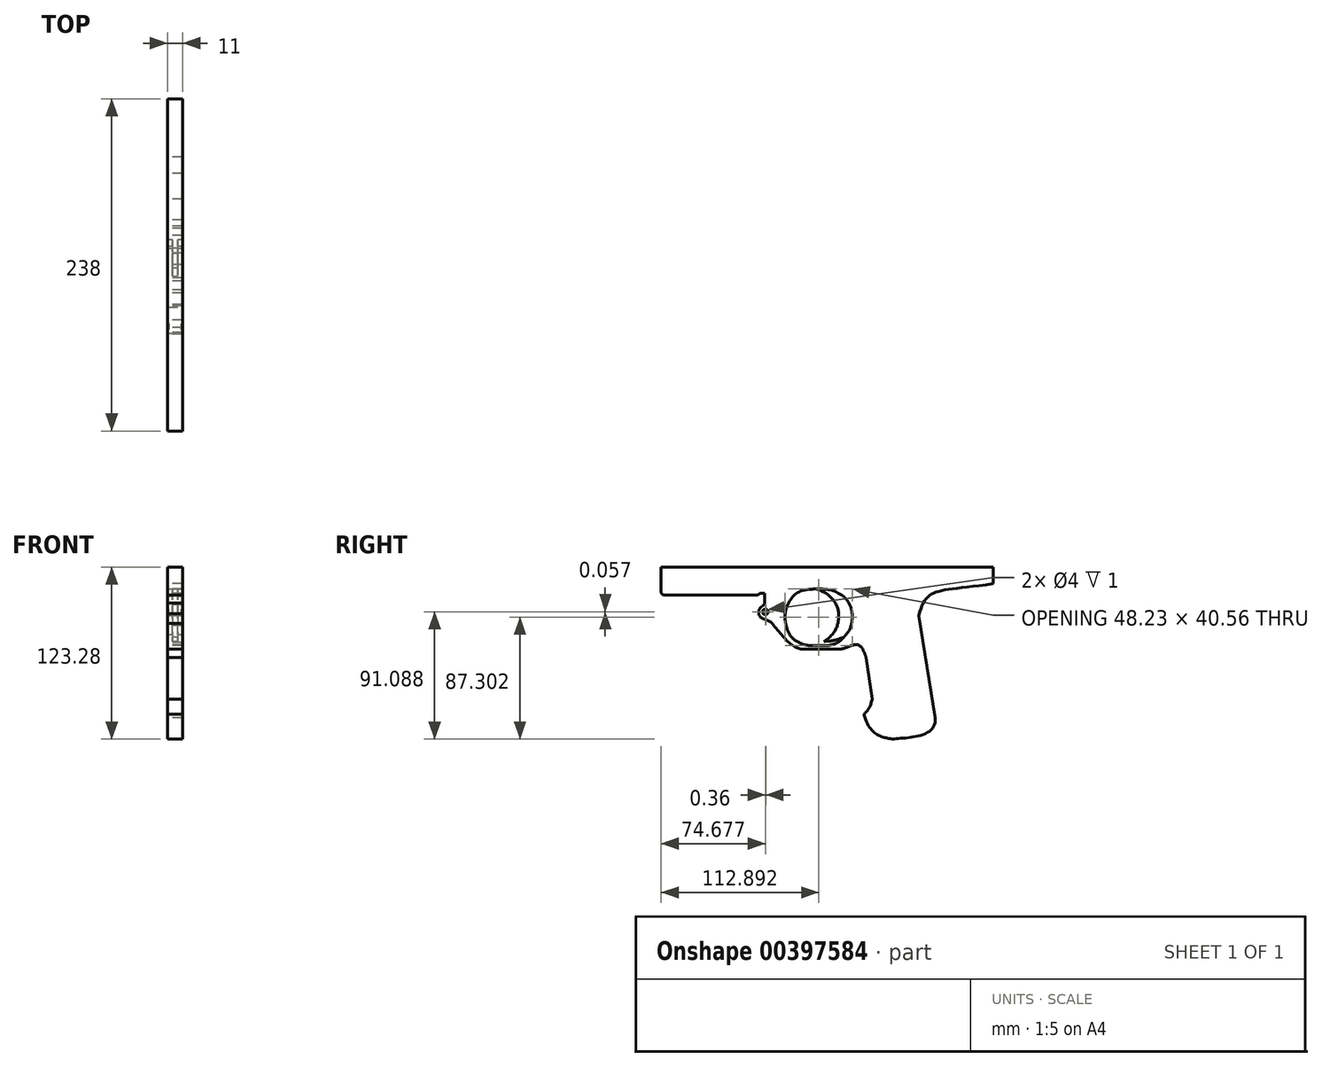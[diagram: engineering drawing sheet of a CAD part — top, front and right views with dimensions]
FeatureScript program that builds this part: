
annotation { "Feature Type Name" : "Feature", "Feature Type Description" : "" }
export const myFeature = defineFeature(function(context is Context, id is Id, definition is map)
    precondition{}
    {
        {
            var Q0;
            Q0=qCreatedBy(makeId("Right.planeOp"),FACE);
            var sketch = newSketch(context, id + "F0", { "sketchPlane" : qUnion([Q0])});
            skLineSegment(sketch, "E0", {"start": v(0, 0) * mm, "end": v(0, -230) * mm});
            skLineSegment(sketch, "E1", {"start": v(0, -230) * mm, "end": v(119.99, -230) * mm});
            skLineSegment(sketch, "E2", {"start": v(0, -230) * mm, "end": v(-112.03, -230) * mm});
            skLineSegment(sketch, "E3", {"start": v(-112.03, -230) * mm, "end": v(125.97, -230) * mm});
            skLineSegment(sketch, "E4.bottom", {"start": v(125.97, -230) * mm, "end": v(-112.03, -230) * mm});
            skLineSegment(sketch, "E4.top", {"start": v(125.97, -218) * mm, "end": v(-112.03, -218) * mm});
            skLineSegment(sketch, "E4.left", {"start": v(125.97, -230) * mm, "end": v(125.97, -218) * mm});
            skLineSegment(sketch, "E4.right", {"start": v(-112.03, -230) * mm, "end": v(-112.03, -218) * mm});
            skLineSegment(sketch, "E5.bottom", {"start": v(-112.03, -230) * mm, "end": v(-42.58, -230) * mm});
            skLineSegment(sketch, "E5.top", {"start": v(-112.03, -238) * mm, "end": v(-42.58, -238) * mm});
            skLineSegment(sketch, "E5.left", {"start": v(-112.03, -230) * mm, "end": v(-112.03, -238) * mm});
            skLineSegment(sketch, "E5.right", {"start": v(-42.58, -230) * mm, "end": v(-42.58, -238) * mm});
            skFitSpline(sketch, "E6", {"points": [v(125.97, -230) * mm, v(72.63, -252.96) * mm], "startDerivative": vector(-124.55, -18.11) * mm, "endDerivative": vector(-16.76, -64.23) * mm});
            skLineSegment(sketch, "E7", {"start": v(72.63, -252.96) * mm, "end": v(84.38, -326.13) * mm});
            skLineSegment(sketch, "E8", {"start": v(72.63, -252.96) * mm, "end": v(30.63, -252.96) * mm});
            skLineSegment(sketch, "E9", {"start": v(30.63, -252.96) * mm, "end": v(39.17, -312.77) * mm});
            skFitSpline(sketch, "E10", {"points": [v(39.17, -312.77) * mm, v(33.3, -323.55) * mm], "startDerivative": vector(-4.85, -23.29) * mm, "endDerivative": vector(-3.71, -4.12) * mm});
            skFitSpline(sketch, "E11", {"points": [v(33.3, -323.55) * mm, v(54.05, -341.28) * mm], "startDerivative": vector(11.13, -45.76) * mm, "endDerivative": vector(21.03, -2.47) * mm});
            skFitSpline(sketch, "E12", {"points": [v(54.05, -341.28) * mm, v(84.38, -326.13) * mm], "startDerivative": vector(26.38, 2.89) * mm, "endDerivative": vector(-5.07, 44.22) * mm});
            skFitSpline(sketch, "E13", {"points": [v(34.9, -282.87) * mm, v(28.31, -273.6) * mm], "startDerivative": vector(-4.14, 7.9) * mm, "endDerivative": vector(-14.15, 4) * mm});
            skFitSpline(sketch, "E14", {"points": [v(28.31, -273.6) * mm, v(15.3, -276.86) * mm], "startDerivative": vector(-16.78, -0.73) * mm, "endDerivative": vector(-15.09, 0.25) * mm});
            skLineSegment(sketch, "E15", {"start": v(15.3, -276.86) * mm, "end": v(-10.85, -276.86) * mm});
            skFitSpline(sketch, "E16", {"points": [v(-10.85, -276.86) * mm, v(-32.4, -258.45) * mm], "startDerivative": vector(-21.55, 1.34) * mm, "endDerivative": vector(-21.06, 27.43) * mm});
            skFitSpline(sketch, "E17", {"points": [v(-32.4, -258.45) * mm, v(-42.03, -251.43) * mm], "startDerivative": vector(-13.71, 13.22) * mm, "endDerivative": vector(-3.43, 15.67) * mm});
            skFitSpline(sketch, "E18", {"points": [v(-42.03, -251.43) * mm, v(-37.79, -243.92) * mm], "startDerivative": vector(-1.47, 16.65) * mm, "endDerivative": vector(1.96, 8.33) * mm});
            skLineSegment(sketch, "E19", {"start": v(-37.79, -243.92) * mm, "end": v(-37.79, -236.74) * mm});
            skLineSegment(sketch, "E20", {"start": v(-37.79, -236.74) * mm, "end": v(-41.22, -236.74) * mm});
            skLineSegment(sketch, "E21", {"start": v(-41.22, -236.74) * mm, "end": v(-42.58, -238) * mm});
            skFitSpline(sketch, "E22", {"points": [v(-2.29, -233.8) * mm, v(-21.4, -245.26) * mm], "startDerivative": vector(-13.28, -0.6) * mm, "endDerivative": vector(-14.49, -35) * mm});
            skFitSpline(sketch, "E23", {"points": [v(-21.4, -245.26) * mm, v(-22.36, -259.94) * mm], "startDerivative": vector(-6.68, -12.56) * mm, "endDerivative": vector(4.15, -12.1) * mm});
            skFitSpline(sketch, "E24", {"points": [v(-22.36, -259.94) * mm, v(-13.25, -272.16) * mm], "startDerivative": vector(3.8, -18.33) * mm, "endDerivative": vector(14.87, -6.57) * mm});
            skFitSpline(sketch, "E25", {"points": [v(-13.25, -272.16) * mm, v(-4.64, -274.26) * mm], "startDerivative": vector(13.14, -6.31) * mm, "endDerivative": vector(7.97, -0.18) * mm});
            skLineSegment(sketch, "E26", {"start": v(-4.64, -274.26) * mm, "end": v(7.27, -274.26) * mm});
            skFitSpline(sketch, "E27", {"points": [v(7.27, -274.26) * mm, v(20.33, -266.59) * mm], "startDerivative": vector(21.47, 2.35) * mm, "endDerivative": vector(8.86, 11) * mm});
            skFitSpline(sketch, "E28", {"points": [v(20.33, -266.59) * mm, v(24.98, -253.08) * mm], "startDerivative": vector(11, 12.08) * mm, "endDerivative": vector(0.54, 16.64) * mm});
            skFitSpline(sketch, "E29", {"points": [v(24.98, -253.08) * mm, v(18.54, -239.13) * mm], "startDerivative": vector(-0.8, 17.17) * mm, "endDerivative": vector(-13.42, 11) * mm});
            skFitSpline(sketch, "E30", {"points": [v(18.54, -239.13) * mm, v(5.48, -233.94) * mm, v(-2.29, -233.8) * mm], "startDerivative": vector(-32.75, 23.86) * mm, "endDerivative": vector(-17.24, -1.5) * mm});
            skFitSpline(sketch, "E31", {"points": [v(-1.16, -233.72) * mm, v(15.15, -252.95) * mm], "startDerivative": vector(40.59, -10.15) * mm, "endDerivative": vector(-2.18, -12.34) * mm});
            skFitSpline(sketch, "E32", {"points": [v(15.15, -252.95) * mm, v(4.76, -271.32) * mm], "startDerivative": vector(0.34, -14.58) * mm, "endDerivative": vector(-28.74, -18.9) * mm});
            skFitSpline(sketch, "E33", {"points": [v(4.76, -271.32) * mm, v(18.88, -268.32) * mm], "startDerivative": vector(9.64, 0.6) * mm, "endDerivative": vector(21.9, 9.22) * mm});
            skSolve(sketch);
        }
        {
            var Q0;
            Q0=qSketchRegion(id+"F0",true);
            extrude(context, id + "F1", {"entities" : qUnion([Q0]), "depth" : 11 * mm});
        }
        {
            var Q0;
            {var subQ3=sQuery(id+"F0.wireOp",EDGE,"E28");Q0=makeQuery(id+"F0.imprint","IMPRINT",FACE,{"disambiguationData":[TD([[makeQuery(id+"F0.imprint","IMPRINT",EDGE,{"derivedFrom":subQ3}),1.0]])]});}
            extrude(context, id + "F2", {"entities" : qUnion([Q0]), "operationType" : NewBodyOperationType.ADD, "depth" : 7.5 * mm});
        }
        {
            var Q0;
            {var subQ3=sQuery(id+"F0.wireOp",EDGE,"E28");Q0=makeQuery(id+"F0.imprint","IMPRINT",FACE,{"disambiguationData":[TD([[makeQuery(id+"F0.imprint","IMPRINT",EDGE,{"derivedFrom":subQ3}),1.0]])]});}
            extrude(context, id + "F3", {"entities" : qUnion([Q0]), "operationType" : NewBodyOperationType.REMOVE, "depth" : 3.5 * mm});
        }
        {
            var Q0;
            Q0=makeQuery(id+"F1.opExtrude","CAP_FACE",FACE,{"disambiguationData":[OSD([sQuery(id+"F0.wireOp",EDGE,"E4.top"),sQuery(id+"F0.wireOp",EDGE,"E4.left"),sQuery(id+"F0.wireOp",EDGE,"E4.right"),sQuery(id+"F0.wireOp",EDGE,"E5.top"),sQuery(id+"F0.wireOp",EDGE,"E5.left"),sQuery(id+"F0.wireOp",EDGE,"E6"),sQuery(id+"F0.wireOp",EDGE,"E7"),sQuery(id+"F0.wireOp",EDGE,"E9"),sQuery(id+"F0.wireOp",EDGE,"E10"),sQuery(id+"F0.wireOp",EDGE,"E11"),sQuery(id+"F0.wireOp",EDGE,"E12"),sQuery(id+"F0.wireOp",EDGE,"E13"),sQuery(id+"F0.wireOp",EDGE,"E14"),sQuery(id+"F0.wireOp",EDGE,"E15"),sQuery(id+"F0.wireOp",EDGE,"E16"),sQuery(id+"F0.wireOp",EDGE,"E17"),sQuery(id+"F0.wireOp",EDGE,"E18"),sQuery(id+"F0.wireOp",EDGE,"E19"),sQuery(id+"F0.wireOp",EDGE,"E20"),sQuery(id+"F0.wireOp",EDGE,"E21"),sQuery(id+"F0.wireOp",EDGE,"E22"),sQuery(id+"F0.wireOp",EDGE,"E23"),sQuery(id+"F0.wireOp",EDGE,"E24"),sQuery(id+"F0.wireOp",EDGE,"E25"),sQuery(id+"F0.wireOp",EDGE,"E26"),sQuery(id+"F0.wireOp",EDGE,"E27"),sQuery(id+"F0.wireOp",EDGE,"E28"),sQuery(id+"F0.wireOp",EDGE,"E29"),sQuery(id+"F0.wireOp",EDGE,"E30")])],"isStart":false});
            var sketch = newSketch(context, id + "F4", { "sketchPlane" : qUnion([Q0])});
            skCircle(sketch, "E34", {"center": v(-37.35, -250.14) * mm, "radius": 2 * mm});
            skSolve(sketch);
        }
        {
            var Q0;
            Q0=qSketchRegion(id+"F4",true);
            extrude(context, id + "F5", {"entities" : qUnion([Q0]), "operationType" : NewBodyOperationType.REMOVE, "oppositeDirection" : true, "depth" : 1 * mm});
        }
        {
            var Q0;
            {var subQ4=sQuery(id+"F0.wireOp",EDGE,"E5.right");Q0=makeQuery(id+"F0.imprint","IMPRINT",FACE,{"disambiguationData":[TD([[makeQuery(id+"F0.imprint","IMPRINT",EDGE,{"derivedFrom":subQ4}),1.0]])]});}
            var sketch = newSketch(context, id + "F6", { "sketchPlane" : qUnion([Q0])});
            skCircle(sketch, "E35", {"center": v(-37, -250.2) * mm, "radius": 2 * mm});
            skSolve(sketch);
        }
        {
            var Q0;
            Q0=qSketchRegion(id+"F6",true);
            extrude(context, id + "F7", {"entities" : qUnion([Q0]), "operationType" : NewBodyOperationType.REMOVE, "depth" : 1 * mm});
        }
        {
            var Q0;
            Q0=makeQuery(id+"F1.opExtrude","SWEPT_EDGE",EDGE,{"disambiguationData":[OSD([sQuery(id+"F0.wireOp",EDGE,"E5.top"),sQuery(id+"F0.wireOp",EDGE,"E5.left")])]});
            fillet(context, id + "F8", {"entities" : qUnion([Q0]), "radius" : 2 * mm, "tangentPropagation" : true, "allowEdgeOverflow" : false});
        }
    });
